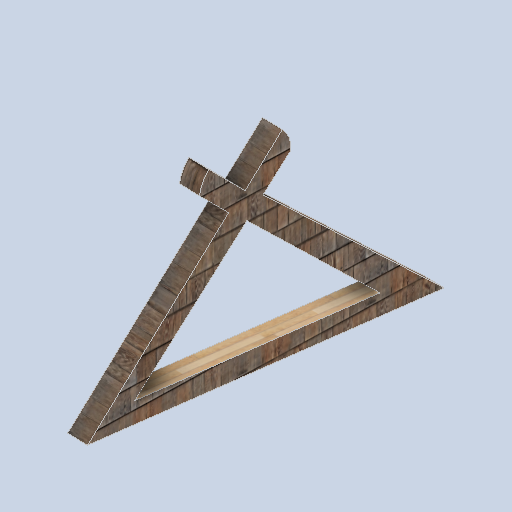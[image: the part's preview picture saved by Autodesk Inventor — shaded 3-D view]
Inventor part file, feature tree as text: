
AUTODESK INVENTOR PART (.ipt)
format: ipt  version: 2024.2 (Build 282272000, 272)  size: 228,352 bytes
history: native  units: in
note: dims shown in document units (in); Inventor stores cm internally (conversion verified against a paired STEP export)
features: sketch x10, plane x8, other x3
ambient origin geometry x8: Origin, YZ Plane, XZ Plane, XY Plane, X Axis, Y Axis, Z Axis, Center Point
bodies: Solid1 (feature_tree)
feature tree (21):
  other  "pad_outframe_02.ipt"
  other  "Solid1::pad_outframe_02.ipt"
  other  "TaggingFeature1"
  sketch  "Sketch1"  dims[d0=0.3937in]
  sketch  "Sketch2"
  sketch  "Sketch3"
  sketch  "Sketch6"
  sketch  "Sketch7"
  sketch  "Sketch8"
  sketch  "Sketch9"
  sketch  "Sketch10"
  sketch  "Sketch11"
  sketch  "Sketch12"
  plane  "Work Plane1"
  plane  "Work Plane2"
  plane  "Work Plane3"
  plane  "Work Plane4"
  plane  "Work Plane5"
  plane  "Work Plane6"
  plane  "Work Plane7"
  plane  "Work Plane8"
